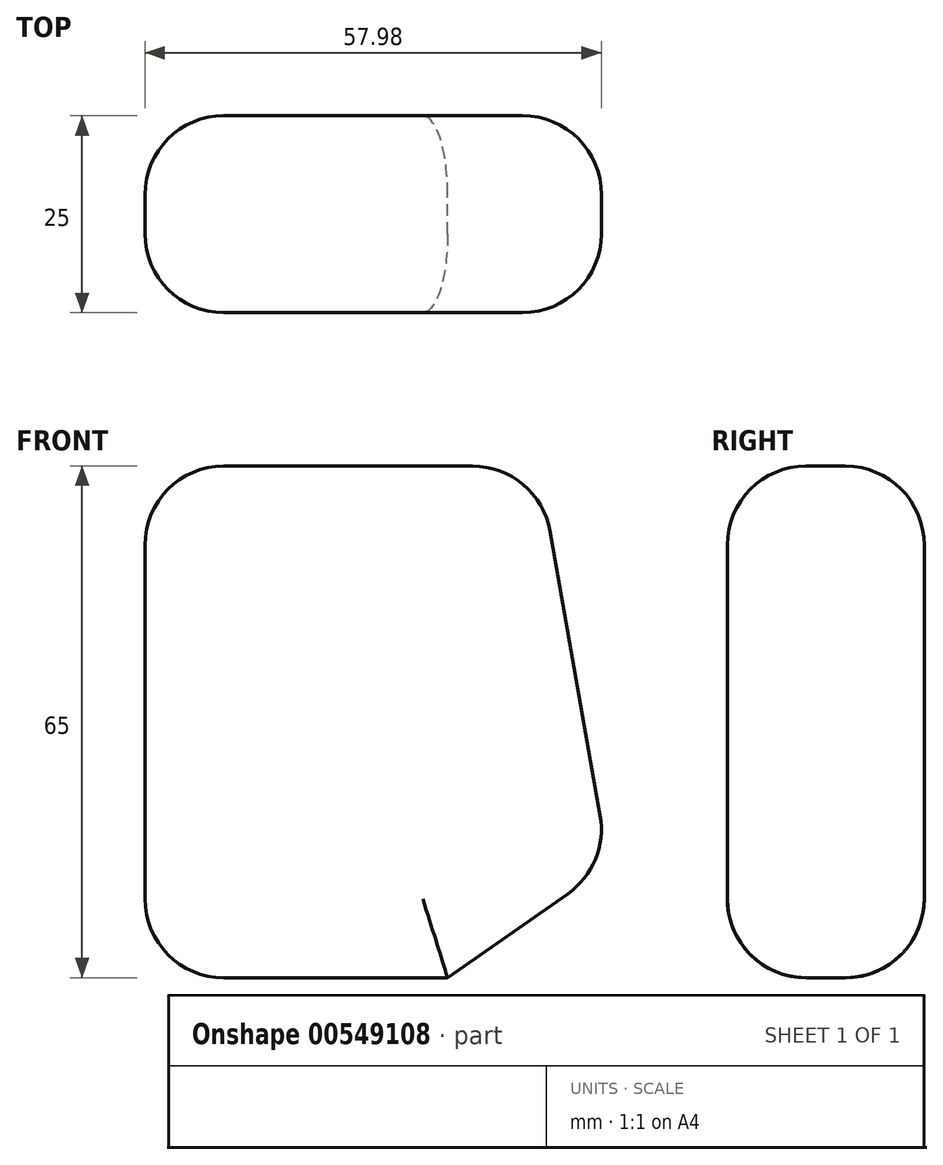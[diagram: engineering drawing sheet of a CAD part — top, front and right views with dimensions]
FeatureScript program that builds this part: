
annotation { "Feature Type Name" : "Feature", "Feature Type Description" : "" }
export const myFeature = defineFeature(function(context is Context, id is Id, definition is map)
    precondition{}
    {
        {
            var Q0;
            Q0=qCreatedBy(makeId("Front.planeOp"),FACE);
            var sketch = newSketch(context, id + "F0", { "sketchPlane" : qUnion([Q0])});
            skLineSegment(sketch, "E0", {"start": v(-26.12, -33.47) * mm, "end": v(-26.12, 31.53) * mm});
            skLineSegment(sketch, "E1", {"start": v(-26.12, 31.53) * mm, "end": v(23.88, 31.53) * mm});
            skLineSegment(sketch, "E2", {"start": v(23.88, 31.53) * mm, "end": v(32.81, -19.13) * mm});
            skLineSegment(sketch, "E3", {"start": v(32.81, -19.13) * mm, "end": v(12.33, -33.47) * mm});
            skLineSegment(sketch, "E4", {"start": v(12.33, -33.47) * mm, "end": v(-26.12, -33.47) * mm});
            skSolve(sketch);
        }
        {
            var Q0;
            Q0=makeQuery(id+"F0.imprint","IMPRINT",FACE,{"disambiguationData":[TD([[makeQuery(id+"F0.imprint","IMPRINT",EDGE,{"derivedFrom":sQuery(id+"F0.wireOp",EDGE,"E0")}),-1.0]])]});
            extrude(context, id + "F1", {"entities" : qUnion([Q0]), "depth" : 25 * mm, "offsetDistance" : 25 * mm});
        }
        {
            var Q0;
            Q0=makeQuery(id+"F1.opExtrude","SWEPT_EDGE",EDGE,{"disambiguationData":[OSD([sQuery(id+"F0.wireOp",EDGE,"E1"),sQuery(id+"F0.wireOp",EDGE,"E2")])]});
            var Q1;
            Q1=makeQuery(id+"F1.opExtrude","SWEPT_EDGE",EDGE,{"disambiguationData":[OSD([sQuery(id+"F0.wireOp",EDGE,"E2"),sQuery(id+"F0.wireOp",EDGE,"E3")])]});
            var Q2;
            Q2=makeQuery(id+"F1.opExtrude","SWEPT_EDGE",EDGE,{"disambiguationData":[OSD([sQuery(id+"F0.wireOp",EDGE,"E0"),sQuery(id+"F0.wireOp",EDGE,"E1")])]});
            var Q3;
            Q3=makeQuery(id+"F1.opExtrude","SWEPT_EDGE",EDGE,{"disambiguationData":[OSD([sQuery(id+"F0.wireOp",EDGE,"E0"),sQuery(id+"F0.wireOp",EDGE,"E4")])]});
            var Q4;
            Q4=makeQuery(id+"F1.opExtrude","CAP_FACE",FACE,{"disambiguationData":[OSD([sQuery(id+"F0.wireOp",EDGE,"E0"),sQuery(id+"F0.wireOp",EDGE,"E1"),sQuery(id+"F0.wireOp",EDGE,"E2"),sQuery(id+"F0.wireOp",EDGE,"E3"),sQuery(id+"F0.wireOp",EDGE,"E4")])],"isStart":false});
            var Q5;
            Q5=makeQuery(id+"F1.opExtrude","CAP_FACE",FACE,{"disambiguationData":[OSD([sQuery(id+"F0.wireOp",EDGE,"E0"),sQuery(id+"F0.wireOp",EDGE,"E1"),sQuery(id+"F0.wireOp",EDGE,"E2"),sQuery(id+"F0.wireOp",EDGE,"E3"),sQuery(id+"F0.wireOp",EDGE,"E4")])],"isStart":true});
            fillet(context, id + "F2", {"entities" : qUnion([Q0, Q1, Q2, Q3, Q4, Q5]), "radius" : 10 * mm, "tangentPropagation" : true, "allowEdgeOverflow" : false});
        }
    });
